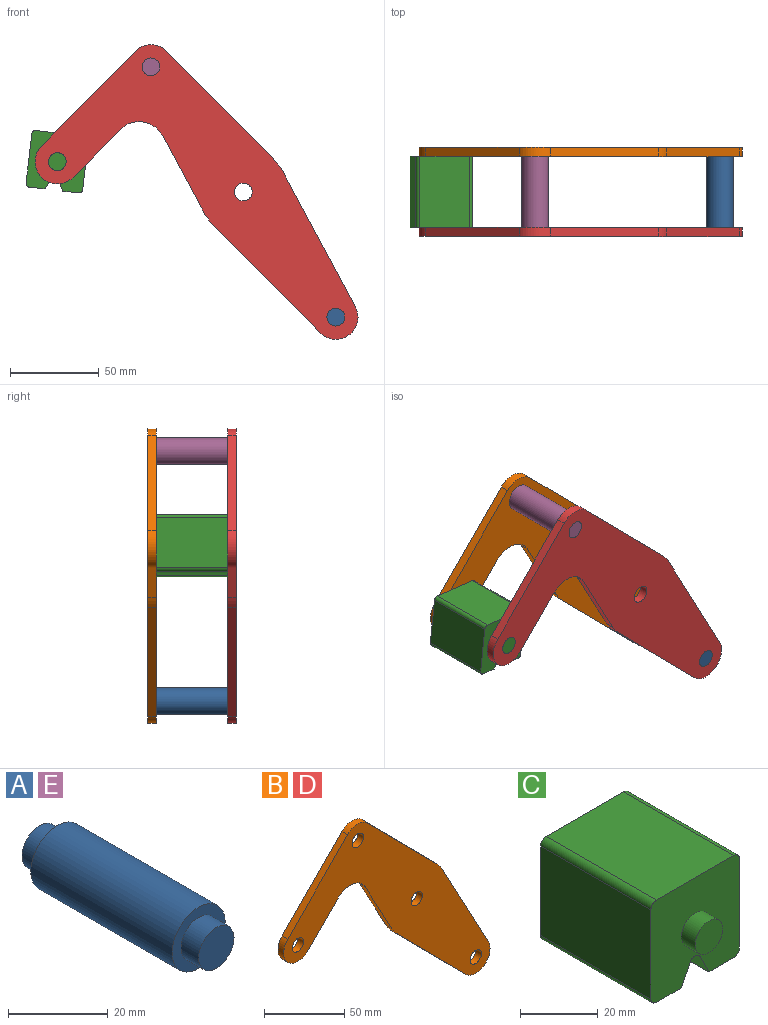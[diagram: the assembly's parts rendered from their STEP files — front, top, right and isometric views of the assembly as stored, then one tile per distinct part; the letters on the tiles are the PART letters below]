
ASSEMBLY  parts=5 mates=3
PART A: 7 faces, bbox 15x50x15 mm
  f0: cylinder r=7.5mm len=40mm, axis (0,-1,0), area 1885mm2, adj f2,f5
  f1: cylinder r=5mm len=10mm, axis (0,1,0), area 157.1mm2, adj f2,f3
  f2: plane 15x15mm, normal (0,-1,0), area 98.2mm2, adj f0,f1
  f3: plane 10x10mm, normal (0,-1,0), area 78.5mm2, adj f1
  f4: cylinder r=5mm len=10mm, axis (0,-1,0), area 157.1mm2, adj f5,f6
  f5: plane 15x15mm, normal (0,1,0), area 98.2mm2, adj f0,f4
  f6: plane 10x10mm, normal (0,1,0), area 78.5mm2, adj f4
PART B: 18 faces, bbox 181.7x5x165.8 mm
  f0: plane 43.49x23.35mm, normal (-0.88,0,-0.47), area 246.8mm2, adj f1,f14,f16,f17
  f1: cylinder r=25mm len=5.75mm, axis (0,1,0), area 35.8mm2, adj f0,f2,f16,f17
  f2: plane 61.6x60.87mm, normal (-0.71,0,-0.7), area 433mm2, adj f1,f3,f16,f17
  f3: cylinder r=12.5mm len=21.39mm, axis (0,1,0), area 178.4mm2, adj f2,f4,f16,f17
  f4: plane 76.3x40.96mm, normal (0.88,0,0.47), area 433mm2, adj f3,f5,f16,f17
  f5: cylinder r=25mm len=5.75mm, axis (0,1,0), area 35.8mm2, adj f4,f6,f16,f17
  f6: plane 61.6x60.87mm, normal (0.71,0,0.7), area 433mm2, adj f5,f7,f16,f17
  f7: cylinder r=12.5mm len=17.78mm, axis (0,1,0), area 98.9mm2, adj f6,f8,f16,f17
  f8: plane 53.35x52.71mm, normal (-0.71,0,0.7), area 375mm2, adj f7,f9,f16,f17
  f9: cylinder r=12.5mm len=21.39mm, axis (0,1,0), area 196.3mm2, adj f8,f10,f16,f17
  f10: plane 26.86x26.54mm, normal (0.71,0,-0.7), area 188.8mm2, adj f9,f14,f16,f17
  f11: cylinder r=5mm len=10mm, axis (0,1,0), area 157.1mm2, adj f16,f17
  f12: cylinder r=5mm len=10mm, axis (0,1,0), area 157.1mm2, adj f16,f17
  f13: cylinder r=5mm len=10mm, axis (0,1,0), area 157.1mm2, adj f16,f17
  f14: cylinder r=15mm len=23.89mm, axis (0,1,0), area 140.2mm2, adj f0,f10,f16,f17
  f15: cylinder r=5mm len=10mm, axis (0,1,0), area 157.1mm2, adj f16,f17
  f16: plane 181.66x165.78mm, normal (0,-1,0), area 8710.1mm2, adj f0,f1,f2,f3,f4,f5,f6,f7
  f17: plane 181.66x165.78mm, normal (0,1,0), area 8710.1mm2, adj f0,f1,f2,f3,f4,f5,f6,f7
PART C: 18 faces, bbox 32.1x50x32.1 mm
  f0: plane 40x28.08mm, normal (1,0,0), area 1123.1mm2, adj f4,f10,f13,f14
  f1: plane 40x9.04mm, normal (0,0,-1), area 361.6mm2, adj f2,f4,f10,f14
  f2: plane 40x6.42mm, normal (-0.89,0,-0.45), area 287.2mm2, adj f1,f4,f10,f15
  f3: plane 40x6.42mm, normal (0.89,0,-0.45), area 287.2mm2, adj f4,f5,f10,f15
  f4: plane 32.08x32.08mm, normal (0,-1,0), area 900.6mm2, adj f0,f1,f2,f3,f5,f6,f7,f9
  f5: plane 40x9.04mm, normal (0,0,-1), area 361.6mm2, adj f3,f4,f10,f16
  f6: plane 40x28.08mm, normal (0,0,1), area 1123.1mm2, adj f4,f10,f13,f17
  f7: plane 40x28.08mm, normal (-1,0,0), area 1123.1mm2, adj f4,f10,f16,f17
  f8: plane 10x10mm, normal (0,-1,0), area 78.5mm2, adj f9
  f9: cylinder r=5mm len=10mm, axis (0,1,0), area 157.1mm2, adj f4,f8
  f10: plane 32.08x32.08mm, normal (0,1,0), area 900.6mm2, adj f0,f1,f2,f3,f5,f6,f7,f12
  f11: plane 10x10mm, normal (0,1,0), area 78.5mm2, adj f12
  f12: cylinder r=5mm len=10mm, axis (0,-1,0), area 157.1mm2, adj f10,f11
  f13: cylinder r=2mm len=40mm, axis (0,1,0), area 125.7mm2, adj f0,f4,f6,f10
  f14: cylinder r=2mm len=40mm, axis (0,-1,0), area 125.7mm2, adj f0,f1,f4,f10
  f15: cylinder r=2mm len=40mm, axis (0,1,0), area 177.1mm2, adj f2,f3,f4,f10
  f16: cylinder r=2mm len=40mm, axis (0,1,0), area 125.7mm2, adj f4,f5,f7,f10
  f17: cylinder r=2mm len=40mm, axis (0,-1,0), area 125.7mm2, adj f4,f6,f7,f10
PART D: same geometry as B
PART E: same geometry as A
PLACE A t=(103.95,-20,-140.78)mm
PLACE B t=(0,25,0)mm
PLACE C rot(axis=(0,1,0),6.7deg) t=(-2.72,-20,-12.14)mm
PLACE D t=(0,-20,0)mm fixed
PLACE E t=(0,-20,0)mm
MATE fastened A.f0 <-> B.f3  axis (0,1,0) through (51.98,20,-70.39)mm
MATE fastened E.f0 <-> B.f7  axis (0,1,0) through (-51.98,25,70.39)mm
MATE revolute C.f9 <-> D.f9  axis (0,-1,0) through (-104.69,-25,17.04)mm
